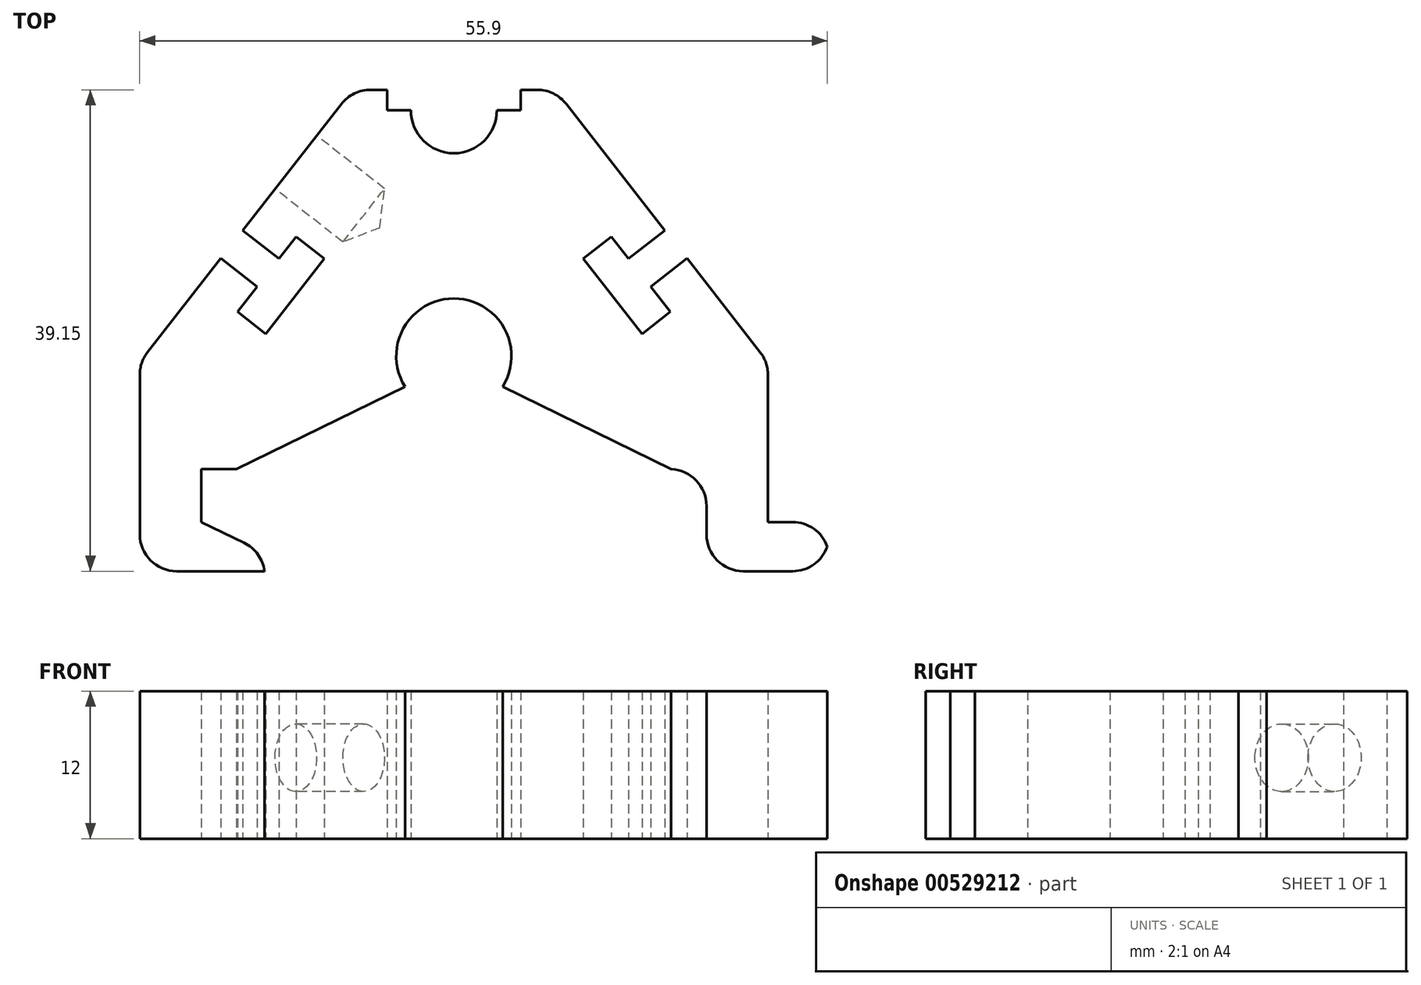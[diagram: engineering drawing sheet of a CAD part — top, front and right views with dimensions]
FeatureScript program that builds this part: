
annotation { "Feature Type Name" : "Feature", "Feature Type Description" : "" }
export const myFeature = defineFeature(function(context is Context, id is Id, definition is map)
    precondition{}
    {
        {
            var Q0;
            Q0=qCreatedBy(makeId("Top.planeOp"),FACE);
            var sketch = newSketch(context, id + "F0", { "sketchPlane" : qUnion([Q0])});
            skLineSegment(sketch, "E0", {"start": v(5.44, 33.49) * mm, "end": v(5.44, 35.15) * mm});
            skLineSegment(sketch, "E1", {"start": v(5.44, 35.15) * mm, "end": v(8.24, 35.15) * mm});
            skLineSegment(sketch, "E2", {"start": v(8.24, 35.15) * mm, "end": v(17.16, 23.72) * mm});
            skLineSegment(sketch, "E3", {"start": v(25.54, 13) * mm, "end": v(25.54, 0) * mm});
            skLineSegment(sketch, "E4", {"start": v(25.54, 0) * mm, "end": v(30.54, 0) * mm});
            skLineSegment(sketch, "E5", {"start": v(30.54, 0) * mm, "end": v(30.54, -4) * mm});
            skLineSegment(sketch, "E6", {"start": v(30.54, -4) * mm, "end": v(20.54, -4) * mm});
            skLineSegment(sketch, "E7", {"start": v(20.54, -4) * mm, "end": v(20.54, 4.3) * mm});
            skLineSegment(sketch, "E8.trimOffspring", {"start": v(3.5, 33.49) * mm, "end": v(5.44, 33.49) * mm});
            skLineSegment(sketch, "E9.MirrorCS", {"start": v(-5.44, 33.49) * mm, "end": v(-5.44, 35.15) * mm});
            skLineSegment(sketch, "E10.MirrorCS", {"start": v(-5.44, 35.15) * mm, "end": v(-8.24, 35.15) * mm});
            skLineSegment(sketch, "E11.MirrorCS", {"start": v(-25.54, -4) * mm, "end": v(-20.54, -4) * mm});
            skLineSegment(sketch, "E12.MirrorCS", {"start": v(-20.54, 0) * mm, "end": v(-20.54, 4.3) * mm});
            skLineSegment(sketch, "E13.MirrorCS", {"start": v(-8.24, 35.15) * mm, "end": v(-17.16, 23.72) * mm});
            skLineSegment(sketch, "E14.MirrorCS", {"start": v(-3.48, 33.49) * mm, "end": v(-5.44, 33.49) * mm});
            skLineSegment(sketch, "E15.MirrorCS", {"start": v(-25.54, 13) * mm, "end": v(-25.54, 0) * mm});
            skLineSegment(sketch, "E16.MirrorCS", {"start": v(-20.54, 4.3) * mm, "end": v(-17.67, 4.3) * mm});
            skLineSegment(sketch, "E17", {"start": v(-17.16, 23.72) * mm, "end": v(-14.2, 21.41) * mm});
            skLineSegment(sketch, "E18", {"start": v(-14.2, 21.41) * mm, "end": v(-12.81, 23.2) * mm});
            skLineSegment(sketch, "E19", {"start": v(-12.81, 23.2) * mm, "end": v(-10.53, 21.41) * mm});
            skLineSegment(sketch, "E20", {"start": v(-16, 19.13) * mm, "end": v(-18.95, 21.43) * mm});
            skLineSegment(sketch, "E21.trimOffspring", {"start": v(-18.95, 21.43) * mm, "end": v(-25.54, 13) * mm});
            skLineSegment(sketch, "E22", {"start": v(-10.53, 21.41) * mm, "end": v(-15.3, 15.3) * mm});
            skLineSegment(sketch, "E23", {"start": v(-16, 19.13) * mm, "end": v(-17.58, 17.09) * mm});
            skLineSegment(sketch, "E24", {"start": v(-17.58, 17.09) * mm, "end": v(-15.3, 15.3) * mm});
            skLineSegment(sketch, "E25.MirrorCS", {"start": v(14.2, 21.41) * mm, "end": v(12.81, 23.2) * mm});
            skLineSegment(sketch, "E26.MirrorCS", {"start": v(12.81, 23.2) * mm, "end": v(10.53, 21.41) * mm});
            skLineSegment(sketch, "E27.MirrorCS", {"start": v(17.58, 17.09) * mm, "end": v(15.3, 15.3) * mm});
            skLineSegment(sketch, "E28.MirrorCS", {"start": v(10.53, 21.41) * mm, "end": v(15.3, 15.3) * mm});
            skLineSegment(sketch, "E29.MirrorCS", {"start": v(16, 19.13) * mm, "end": v(17.58, 17.09) * mm});
            skLineSegment(sketch, "E30.MirrorCS", {"start": v(18.95, 21.43) * mm, "end": v(25.54, 13) * mm});
            skLineSegment(sketch, "E31.MirrorCS", {"start": v(16, 19.13) * mm, "end": v(18.95, 21.43) * mm});
            skLineSegment(sketch, "E32.MirrorCS", {"start": v(17.16, 23.72) * mm, "end": v(14.2, 21.41) * mm});
            skPoint(sketch, "E33.orphan", {"position": v(0, 33.49) * mm});
            skArc(sketch, "E34", {"start": v(-3.5, 33.49) * mm, "mid": v(0, 29.99) * mm, "end": v(3.5, 33.49) * mm});
            skPoint(sketch, "E35.orphan", {"position": v(2.72, 33.49) * mm});
            skPoint(sketch, "E36.MirrorCS.start.orphan", {"position": v(-30.54, 0) * mm});
            skLineSegment(sketch, "E37", {"start": v(-25.54, 0) * mm, "end": v(-25.54, -4) * mm});
            skPoint(sketch, "E38.orphan", {"position": v(-30.54, -4) * mm});
            skLineSegment(sketch, "E39", {"start": v(-20.54, -4) * mm, "end": v(-15.39, -4) * mm});
            skLineSegment(sketch, "E40", {"start": v(-15.39, -4) * mm, "end": v(-15.39, -2.52) * mm});
            skLineSegment(sketch, "E41", {"start": v(-15.39, -2.52) * mm, "end": v(-20.54, 0) * mm});
            skArc(sketch, "E42", {"start": v(3.96, 11) * mm, "mid": v(0, 18.17) * mm, "end": v(-3.96, 11) * mm});
            skPoint(sketch, "E43.visualSharp", {"position": v(-3.96, 11) * mm});
            skPoint(sketch, "E44.visualSharp", {"position": v(3.96, 11) * mm});
            skLineSegment(sketch, "E45", {"start": v(-17.67, 4.3) * mm, "end": v(-3.96, 11) * mm});
            skLineSegment(sketch, "E46.MirrorCS", {"start": v(17.67, 4.3) * mm, "end": v(3.96, 11) * mm});
            skLineSegment(sketch, "E47.MirrorCS", {"start": v(20.54, 4.3) * mm, "end": v(17.67, 4.3) * mm});
            skSolve(sketch);
        }
        {
            var Q0;
            Q0=makeQuery(id+"F0.imprint","IMPRINT",FACE,{"disambiguationData":[TD([[makeQuery(id+"F0.imprint","IMPRINT",EDGE,{"derivedFrom":sQuery(id+"F0.wireOp",EDGE,"H41homhS-gmHu-m05J-6xCB-Sal3FximWGmY")}),-1.0]])]});
            var Q1;
            {var subQ4=sQuery(id+"F0.wireOp",EDGE,"E0");Q1=makeQuery(id+"F0.imprint","IMPRINT",FACE,{"disambiguationData":[TD([[makeQuery(id+"F0.imprint","IMPRINT",EDGE,{"derivedFrom":subQ4}),-1.0]])]});}
            extrude(context, id + "F1", {"entities" : qUnion([Q0, Q1]), "depth" : 12 * mm, "offsetDistance" : 25 * mm});
        }
        {
            var Q0;
            Q0=makeQuery(id+"F1.opExtrude","SWEPT_FACE",FACE,{"disambiguationData":[OSD([sQuery(id+"F0.wireOp",EDGE,"E13.MirrorCS")])]});
            var sketch = newSketch(context, id + "F2", { "sketchPlane" : qUnion([Q0])});
            skPoint(sketch, "E48", {"position": v(-15.14, 6.59) * mm});
            skSolve(sketch);
        }
        {
            var Q0;
            Q0=sQuery(id+"F2.wireOp",VERTEX,"E48");
            var Q1;
            Q1=makeQuery(id+"F1.opExtrude","SWEPT_BODY",BODY,{"disambiguationData":[OSD([sQuery(id+"F0.wireOp",EDGE,"E0"),sQuery(id+"F0.wireOp",EDGE,"E1"),sQuery(id+"F0.wireOp",EDGE,"E3"),sQuery(id+"F0.wireOp",EDGE,"E4"),sQuery(id+"F0.wireOp",EDGE,"E5"),sQuery(id+"F0.wireOp",EDGE,"E6"),sQuery(id+"F0.wireOp",EDGE,"E7"),sQuery(id+"F0.wireOp",EDGE,"yqWppwLh-rKKj-Nyjt-eyhW-y5rwTKhMclgN"),sQuery(id+"F0.wireOp",EDGE,"uXYxRg5X-YOiC-vD95-Sq5M-jwLbdIaaFUeh"),sQuery(id+"F0.wireOp",EDGE,"E8.trimOffspring"),sQuery(id+"F0.wireOp",EDGE,"E9.MirrorCS"),sQuery(id+"F0.wireOp",EDGE,"E10.MirrorCS"),sQuery(id+"F0.wireOp",EDGE,"E11.MirrorCS"),sQuery(id+"F0.wireOp",EDGE,"E12.MirrorCS"),sQuery(id+"F0.wireOp",EDGE,"E13.MirrorCS"),sQuery(id+"F0.wireOp",EDGE,"cbd3d107-dd72-4ae2-a53c-50ba477c6e6a5.MirrorCS"),sQuery(id+"F0.wireOp",EDGE,"E14.MirrorCS"),sQuery(id+"F0.wireOp",EDGE,"cbd3d107-dd72-4ae2-a53c-50ba477c6e6a7.MirrorCS"),sQuery(id+"F0.wireOp",EDGE,"E36.MirrorCS"),sQuery(id+"F0.wireOp",EDGE,"E15.MirrorCS"),sQuery(id+"F0.wireOp",EDGE,"E16.MirrorCS"),sQuery(id+"F0.wireOp",EDGE,"fse6yEHb-JKeR-C7UX-4hlK-xKf9UI9rtEuT"),sQuery(id+"F0.wireOp",EDGE,"wT93PPqV-Gtzg-trhd-sbrI-tYHicJrfntRd"),sQuery(id+"F0.wireOp",EDGE,"E17"),sQuery(id+"F0.wireOp",EDGE,"E18"),sQuery(id+"F0.wireOp",EDGE,"E19"),sQuery(id+"F0.wireOp",EDGE,"E20"),sQuery(id+"F0.wireOp",EDGE,"E21.trimOffspring"),sQuery(id+"F0.wireOp",EDGE,"E22"),sQuery(id+"F0.wireOp",EDGE,"E23"),sQuery(id+"F0.wireOp",EDGE,"E24"),sQuery(id+"F0.wireOp",EDGE,"E25.MirrorCS"),sQuery(id+"F0.wireOp",EDGE,"E26.MirrorCS"),sQuery(id+"F0.wireOp",EDGE,"E27.MirrorCS"),sQuery(id+"F0.wireOp",EDGE,"E28.MirrorCS"),sQuery(id+"F0.wireOp",EDGE,"E29.MirrorCS"),sQuery(id+"F0.wireOp",EDGE,"E31.MirrorCS"),sQuery(id+"F0.wireOp",EDGE,"E2"),sQuery(id+"F0.wireOp",EDGE,"E32.MirrorCS"),sQuery(id+"F0.wireOp",EDGE,"E30.MirrorCS")])]});
            hole(context, id + "F3", {"style" : HoleStyle.SIMPLE, "endStyle" : HoleEndStyle.BLIND, "standardTappedOrClearance" : lookupTablePath({ "standard" : "ISO", "fit" : "Normal", "size" : "M5", "type" : "Clearance" }), "standardBlindInLast" : lookupTablePath({ "fit" : "Standard", "standard" : "ISO", "size" : "M5", "type" : "Clearance" }), "holeDiameter" : 5.5 * mm, "majorDiameter" : 5 * mm, "holeDepth" : 7 * mm, "isTappedThrough" : true, "tappedDepth" : 12 * mm, "tapClearance" : 3, "startFromSketch" : true, "locations" : qUnion([Q0]), "scope" : qUnion([Q1])});
        }
        {
            var Q0;
            Q0=makeQuery(id+"F1.opExtrude","SWEPT_EDGE",EDGE,{"disambiguationData":[OSD([sQuery(id+"F0.wireOp",EDGE,"E7"),sQuery(id+"F0.wireOp",EDGE,"yqWppwLh-rKKj-Nyjt-eyhW-y5rwTKhMclgN")])]});
            var Q1;
            Q1=makeQuery(id+"F1.opExtrude","SWEPT_EDGE",EDGE,{"disambiguationData":[OSD([sQuery(id+"F0.wireOp",EDGE,"E6"),sQuery(id+"F0.wireOp",EDGE,"E7")])]});
            var Q2;
            Q2=makeQuery(id+"F1.opExtrude","SWEPT_EDGE",EDGE,{"disambiguationData":[OSD([sQuery(id+"F0.wireOp",EDGE,"E3"),sQuery(id+"F0.wireOp",EDGE,"E30.MirrorCS")])]});
            var Q3;
            Q3=makeQuery(id+"F1.opExtrude","SWEPT_EDGE",EDGE,{"disambiguationData":[OSD([sQuery(id+"F0.wireOp",EDGE,"E1"),sQuery(id+"F0.wireOp",EDGE,"E2")])]});
            var Q4;
            Q4=makeQuery(id+"F1.opExtrude","SWEPT_EDGE",EDGE,{"disambiguationData":[OSD([sQuery(id+"F0.wireOp",EDGE,"E15.MirrorCS"),sQuery(id+"F0.wireOp",EDGE,"E21.trimOffspring")])]});
            var Q5;
            Q5=makeQuery(id+"F1.opExtrude","SWEPT_EDGE",EDGE,{"disambiguationData":[OSD([sQuery(id+"F0.wireOp",EDGE,"E11.MirrorCS"),sQuery(id+"F0.wireOp",EDGE,"E37")])]});
            var Q6;
            Q6=makeQuery(id+"F1.opExtrude","SWEPT_EDGE",EDGE,{"disambiguationData":[OSD([sQuery(id+"F0.wireOp",EDGE,"E40"),sQuery(id+"F0.wireOp",EDGE,"E41")])]});
            var Q7;
            Q7=makeQuery(id+"F1.opExtrude","SWEPT_EDGE",EDGE,{"disambiguationData":[OSD([sQuery(id+"F0.wireOp",EDGE,"E4"),sQuery(id+"F0.wireOp",EDGE,"E5")])]});
            var Q8;
            Q8=makeQuery(id+"F1.opExtrude","SWEPT_EDGE",EDGE,{"disambiguationData":[OSD([sQuery(id+"F0.wireOp",EDGE,"E5"),sQuery(id+"F0.wireOp",EDGE,"E6")])]});
            var Q9;
            Q9=makeQuery(id+"F1.opExtrude","SWEPT_EDGE",EDGE,{"disambiguationData":[OSD([sQuery(id+"F0.wireOp",EDGE,"E10.MirrorCS"),sQuery(id+"F0.wireOp",EDGE,"E13.MirrorCS")])]});
            fillet(context, id + "F4", {"entities" : qUnion([Q0, Q1, Q2, Q3, Q4, Q5, Q6, Q7, Q8, Q9]), "radius" : 3 * mm, "tangentPropagation" : true, "allowEdgeOverflow" : false});
        }
    });
